# Revit family: QF_TRUE_TSSU-27-08D-2-HC
name_source: partatom
category: Specialty Equipment
revit_build: Autodesk Revit 2016 (Build: 20150714_1515(x64)
units: mm (PartAtom-declared; Revit-internal decimal feet)

## family parameters
Always vertical = Yes
Cut with Voids When Loaded = No
Part Type = Normal
Room Calculation Point = No
Round Connector Dimension = Use Diameter
Shared = Yes
Work Plane-Based = No

## types (1)
- QF_TRUE_TSSU-27-08D-2-HC
    Apparent Power = 403 VA
    Conn Conduit = Yes
    Conn Plug = NEMA 5-15P
    Cycle = 60 Hz
    Depth = 31 1/16"
    Description = DRAWERED SANDWICH/SALAD UNIT WITH HYDROCARBON REFRIGERANT
    FL Amps = 4 A
    HP = 1/5
    Height = 42 15/16"
    Length = 27 9/16"
    Manufacturer = TRUE
    Max Overcurrent Protection = 0 A
    Min Ckt Ampacity = 0 A
    Model = TSSU-27-08D-2-HC
    Phase = 1
    URL = www.truemfg.com
    URL Cutsheet = www.truemfg.com
    Volts = 115 V
    Watts = 403 W
    Weight in Pounds = 225

## geometry (parser evidence)
native form markers: Blend x90, Sweep x9
no freeform markers — native parametric forms only
